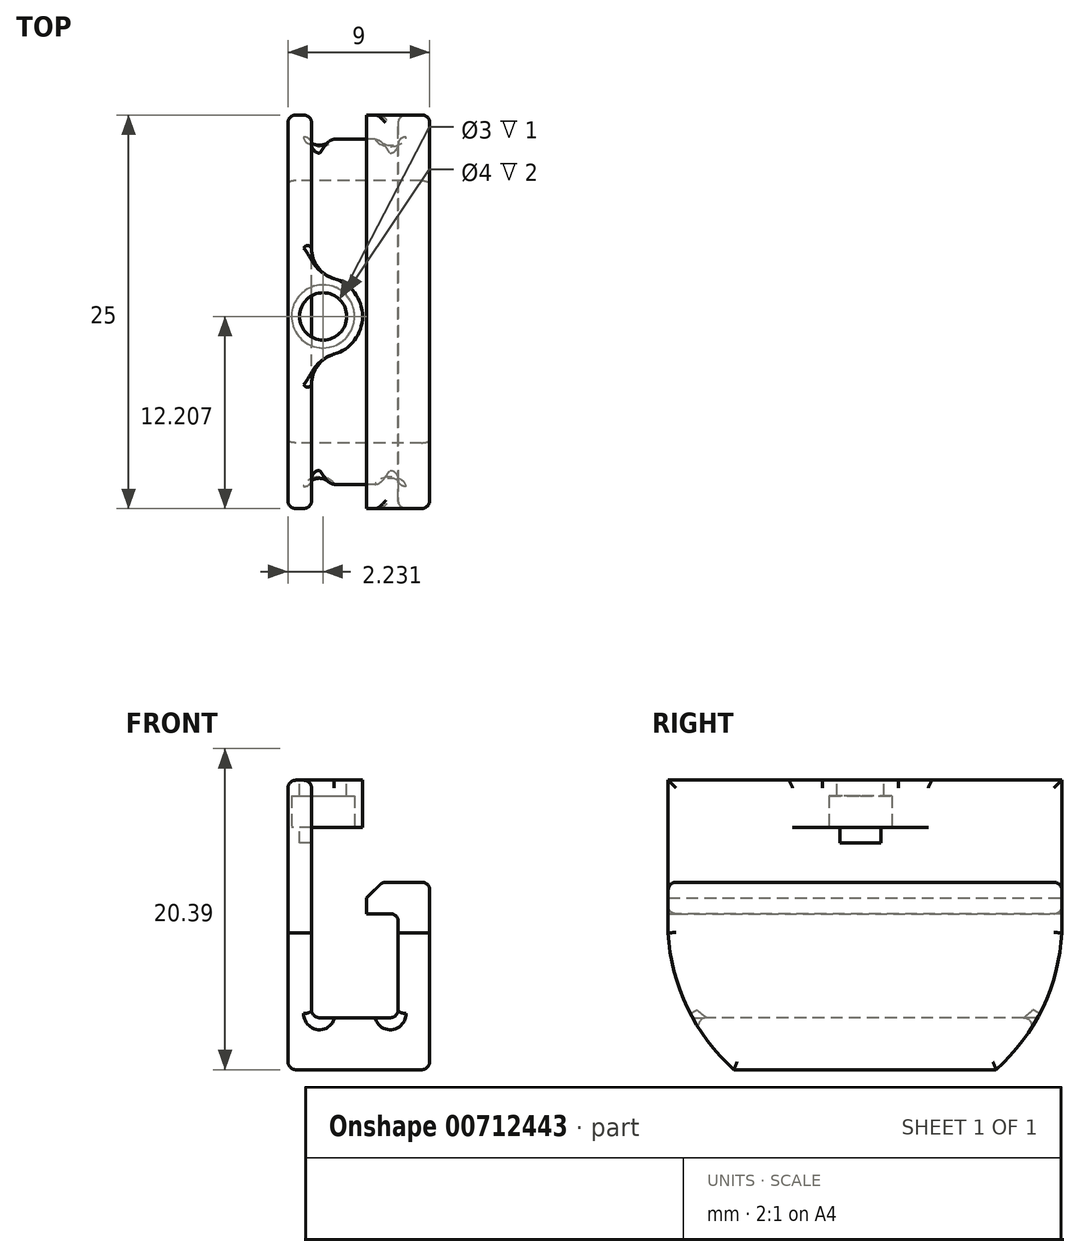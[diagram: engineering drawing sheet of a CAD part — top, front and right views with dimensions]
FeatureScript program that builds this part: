
annotation { "Feature Type Name" : "Feature", "Feature Type Description" : "" }
export const myFeature = defineFeature(function(context is Context, id is Id, definition is map)
    precondition{}
    {
        {
            var Q0;
            Q0=qCreatedBy(makeId("Top.planeOp"),FACE);
            var sketch = newSketch(context, id + "F0", { "sketchPlane" : qUnion([Q0])});
            skCircle(sketch, "E0", {"center": v(0, 0) * mm, "radius": 3.5 * mm});
            skSolve(sketch);
        }
        {
            var Q0;
            Q0 = qSketchRegion(id + "F0", true);
            extrude(context, id + "F1", {"entities" : qUnion([Q0]), "depth" : 15 * mm, "offsetDistance" : 25 * mm});
        }
        {
            var Q0;
            Q0=makeQuery(id+"F1.opExtrude","CAP_FACE",FACE,{"disambiguationData":[OSD([sQuery(id+"F0.wireOp",EDGE,"E0")])],"isStart":false});
            var sketch = newSketch(context, id + "F2", { "sketchPlane" : qUnion([Q0])});
            skCircle(sketch, "E1", {"center": v(0, 0) * mm, "radius": 1.6 * mm});
            skSolve(sketch);
        }
        {
            var Q0;
            Q0 = qSketchRegion(id + "F2", true);
            extrude(context, id + "F3", {"entities" : qUnion([Q0]), "operationType" : NewBodyOperationType.REMOVE, "oppositeDirection" : true, "depth" : 25 * mm, "offsetDistance" : 25 * mm});
        }
        {
            var Q0;
            Q0=makeQuery(id+"F1.opExtrude","CAP_FACE",FACE,{"disambiguationData":[OSD([sQuery(id+"F0.wireOp",EDGE,"E0")])],"isStart":false});
            var sketch = newSketch(context, id + "F4", { "sketchPlane" : qUnion([Q0])});
            skLineSegment(sketch, "E2.bottom", {"start": v(3.28, 0) * mm, "end": v(12.28, 0) * mm});
            skLineSegment(sketch, "E2.top", {"start": v(3.28, -12.5) * mm, "end": v(12.28, -12.5) * mm});
            skLineSegment(sketch, "E2.left", {"start": v(3.28, 0) * mm, "end": v(3.28, -12.5) * mm});
            skLineSegment(sketch, "E2.right", {"start": v(12.28, 0) * mm, "end": v(12.28, -12.5) * mm});
            skLineSegment(sketch, "E3.top", {"start": v(3.28, 12.5) * mm, "end": v(12.28, 12.5) * mm});
            skLineSegment(sketch, "E3.left", {"start": v(3.28, 0) * mm, "end": v(3.28, 12.5) * mm});
            skLineSegment(sketch, "E3.right", {"start": v(12.28, 0) * mm, "end": v(12.28, 12.5) * mm});
            skSolve(sketch);
        }
        {
            var Q0;
            Q0 = qSketchRegion(id + "F4", true);
            extrude(context, id + "F5", {"entities" : qUnion([Q0]), "operationType" : NewBodyOperationType.ADD, "oppositeDirection" : true, "depth" : 25 * mm, "offsetDistance" : 25 * mm});
        }
        {
            var Q0;
            Q0=makeQuery(id+"F5.boolean.opBoolean","INTERSECT",EDGE,{"disambiguationData":[OD(1.0)],"derivedFrom":[makeQuery(id+"F1.opExtrude","SWEPT_FACE",FACE,{"disambiguationData":[OSD([sQuery(id+"F0.wireOp",EDGE,"E0")])]}),makeQuery(id+"F5.opExtrude","SWEPT_FACE",FACE,{"disambiguationData":[OSD([sQuery(id+"F4.wireOp",EDGE,"E2.left"),sQuery(id+"F4.wireOp",EDGE,"E3.left")])]})]});
            var Q1;
            Q1=makeQuery(id+"F5.boolean.opBoolean","INTERSECT",EDGE,{"disambiguationData":[OD(0.0)],"derivedFrom":[makeQuery(id+"F1.opExtrude","SWEPT_FACE",FACE,{"disambiguationData":[OSD([sQuery(id+"F0.wireOp",EDGE,"E0")])]}),makeQuery(id+"F5.opExtrude","SWEPT_FACE",FACE,{"disambiguationData":[OSD([sQuery(id+"F4.wireOp",EDGE,"E2.left"),sQuery(id+"F4.wireOp",EDGE,"E3.left")])]})]});
            fillet(context, id + "F6", {"entities" : qUnion([Q0, Q1]), "radius" : 5 * mm, "tangentPropagation" : true, "allowEdgeOverflow" : false});
        }
        {
            var Q0;
            Q0=makeQuery(id+"F1.opExtrude","CAP_FACE",FACE,{"disambiguationData":[OSD([sQuery(id+"F0.wireOp",EDGE,"E0")])],"isStart":true});
            var sketch = newSketch(context, id + "F7", { "sketchPlane" : qUnion([Q0])});
            skCircle(sketch, "E4", {"center": v(0, 0) * mm, "radius": 2.5 * mm});
            skSolve(sketch);
        }
        {
            var Q0;
            Q0 = qSketchRegion(id + "F7", true);
            extrude(context, id + "F8", {"entities" : qUnion([Q0]), "operationType" : NewBodyOperationType.REMOVE, "oppositeDirection" : true, "depth" : 5 * mm, "offsetDistance" : 25 * mm});
        }
        {
            var Q0;
            Q0=makeQuery(id+"F5.opExtrude","SWEPT_FACE",FACE,{"disambiguationData":[OSD([sQuery(id+"F4.wireOp",EDGE,"E2.left"),sQuery(id+"F4.wireOp",EDGE,"E3.left")])]});
            var sketch = newSketch(context, id + "F9", { "sketchPlane" : qUnion([Q0])});
            skArc(sketch, "E5", {"start": v(-12.5, 0) * mm, "mid": v(-11.55, -5.48) * mm, "end": v(-8.32, -10) * mm});
            skArc(sketch, "E6", {"start": v(8.32, -10) * mm, "mid": v(11.55, -5.48) * mm, "end": v(12.5, 0) * mm});
            skLineSegment(sketch, "E7", {"start": v(-12.5, 0) * mm, "end": v(-12.5, -10) * mm});
            skLineSegment(sketch, "E8", {"start": v(-12.5, -10) * mm, "end": v(-8.32, -10) * mm});
            skLineSegment(sketch, "E9", {"start": v(12.5, 0) * mm, "end": v(12.5, -10) * mm});
            skLineSegment(sketch, "E10", {"start": v(12.5, -10) * mm, "end": v(8.32, -10) * mm});
            skSolve(sketch);
        }
        {
            var Q0;
            Q0 = qSketchRegion(id + "F9", true);
            extrude(context, id + "F10", {"entities" : qUnion([Q0]), "operationType" : NewBodyOperationType.REMOVE, "oppositeDirection" : true, "depth" : 25 * mm, "offsetDistance" : 25 * mm});
        }
        {
            var Q0;
            Q0=makeQuery(id+"F5.boolean.opBoolean","MERGE",FACE,{"derivedFrom":[makeQuery(id+"F1.opExtrude","CAP_FACE",FACE,{"disambiguationData":[OSD([sQuery(id+"F0.wireOp",EDGE,"E0")])],"isStart":false}),makeQuery(id+"F5.opExtrude","CAP_FACE",FACE,{"disambiguationData":[OSD([sQuery(id+"F4.wireOp",EDGE,"E2.top"),sQuery(id+"F4.wireOp",EDGE,"E2.left"),sQuery(id+"F4.wireOp",EDGE,"E2.right"),sQuery(id+"F4.wireOp",EDGE,"E3.top"),sQuery(id+"F4.wireOp",EDGE,"E3.left"),sQuery(id+"F4.wireOp",EDGE,"E3.right")])],"isStart":true})]});
            var sketch = newSketch(context, id + "F11", { "sketchPlane" : qUnion([Q0])});
            skLineSegment(sketch, "E11.bottom", {"start": v(4.78, 12.5) * mm, "end": v(10.28, 12.5) * mm});
            skLineSegment(sketch, "E11.top", {"start": v(4.78, -12.5) * mm, "end": v(10.28, -12.5) * mm});
            skLineSegment(sketch, "E11.left", {"start": v(4.78, 12.5) * mm, "end": v(4.78, -12.5) * mm});
            skLineSegment(sketch, "E11.right", {"start": v(10.28, 12.5) * mm, "end": v(10.28, -12.5) * mm});
            skSolve(sketch);
        }
        {
            var Q0;
            Q0 = qSketchRegion(id + "F11", true);
            extrude(context, id + "F12", {"entities" : qUnion([Q0]), "operationType" : NewBodyOperationType.REMOVE, "oppositeDirection" : true, "depth" : 21.7 * mm, "offsetDistance" : 25 * mm});
        }
        {
            var Q0;
            Q0=makeQuery(id+"F5.opExtrude","SWEPT_FACE",FACE,{"disambiguationData":[OSD([sQuery(id+"F4.wireOp",EDGE,"E2.right"),sQuery(id+"F4.wireOp",EDGE,"E3.right")])]});
            var sketch = newSketch(context, id + "F13", { "sketchPlane" : qUnion([Q0])});
            skLineSegment(sketch, "E12.bottom", {"start": v(-12.5, 15) * mm, "end": v(12.5, 15) * mm});
            skLineSegment(sketch, "E12.top", {"start": v(-12.5, 1.9) * mm, "end": v(12.5, 1.9) * mm});
            skLineSegment(sketch, "E12.left", {"start": v(-12.5, 15) * mm, "end": v(-12.5, 1.9) * mm});
            skLineSegment(sketch, "E12.right", {"start": v(12.5, 15) * mm, "end": v(12.5, 1.9) * mm});
            skSolve(sketch);
        }
        {
            var Q0;
            Q0 = qSketchRegion(id + "F13", true);
            extrude(context, id + "F14", {"entities" : qUnion([Q0]), "operationType" : NewBodyOperationType.REMOVE, "oppositeDirection" : true, "depth" : 3 * mm, "offsetDistance" : 25 * mm});
        }
        {
            var Q0;
            {var subQ5=sQuery(id+"F4.wireOp",EDGE,"E2.top");Q0=makeQuery(id+"F12.boolean.opBoolean","SPLIT",FACE,{"disambiguationData":[TD([makeQuery(id+"F12.opExtrude","SWEPT_FACE",FACE,{"disambiguationData":[OSD([sQuery(id+"F11.wireOp",EDGE,"E11.right")])]})])],"derivedFrom":makeQuery(id+"F5.opExtrude","SWEPT_FACE",FACE,{"disambiguationData":[OSD([subQ5])]})});}
            var sketch = newSketch(context, id + "F15", { "sketchPlane" : qUnion([Q0])});
            skLineSegment(sketch, "E13.bottom", {"start": v(12.28, 1.9) * mm, "end": v(8.28, 1.9) * mm});
            skLineSegment(sketch, "E13.top", {"start": v(12.28, -0.1) * mm, "end": v(8.28, -0.1) * mm});
            skLineSegment(sketch, "E13.left", {"start": v(12.28, 1.9) * mm, "end": v(12.28, -0.1) * mm});
            skLineSegment(sketch, "E13.right", {"start": v(8.28, 1.9) * mm, "end": v(8.28, -0.1) * mm});
            skSolve(sketch);
        }
        {
            var Q0;
            Q0 = qSketchRegion(id + "F15", true);
            extrude(context, id + "F16", {"entities" : qUnion([Q0]), "operationType" : NewBodyOperationType.ADD, "oppositeDirection" : true, "depth" : 25 * mm, "offsetDistance" : 25 * mm});
        }
        {
            var Q0;
            Q0=makeQuery(id+"F16.opExtrude","SWEPT_EDGE",EDGE,{"disambiguationData":[OSD([sQuery(id+"F15.wireOp",EDGE,"E13.bottom"),sQuery(id+"F15.wireOp",EDGE,"E13.right")])]});
            chamfer(context, id + "F17", {"entities" : qUnion([Q0]), "width" : 1 * mm, "tangentPropagation" : true});
        }
        {
            var Q0;
            {var subQ2=sQuery(id+"F4.wireOp",EDGE,"E3.top");Q0=makeQuery(id+"F12.boolean.opBoolean","SPLIT",FACE,{"disambiguationData":[TD([makeQuery(id+"F12.opExtrude","SWEPT_FACE",FACE,{"disambiguationData":[OSD([sQuery(id+"F11.wireOp",EDGE,"E11.left")])]})])],"derivedFrom":makeQuery(id+"F5.opExtrude","SWEPT_FACE",FACE,{"disambiguationData":[OSD([subQ2])]})});}
            var sketch = newSketch(context, id + "F18", { "sketchPlane" : qUnion([Q0])});
            skLineSegment(sketch, "E14.bottom", {"start": v(-7.78, 16.39) * mm, "end": v(8.9, 16.39) * mm});
            skLineSegment(sketch, "E14.top", {"start": v(-7.78, 8.39) * mm, "end": v(8.9, 8.39) * mm});
            skLineSegment(sketch, "E14.left", {"start": v(-7.78, 16.39) * mm, "end": v(-7.78, 8.39) * mm});
            skLineSegment(sketch, "E14.right", {"start": v(8.9, 16.39) * mm, "end": v(8.9, 8.39) * mm});
            skSolve(sketch);
        }
        {
            var Q0;
            Q0 = qSketchRegion(id + "F18", true);
            extrude(context, id + "F19", {"entities" : qUnion([Q0]), "operationType" : NewBodyOperationType.REMOVE, "oppositeDirection" : true, "depth" : 25 * mm, "offsetDistance" : 25 * mm});
        }
        {
            var Q0;
            Q0=makeQuery(id+"F5.opExtrude","CAP_EDGE",EDGE,{"disambiguationData":[OSD([sQuery(id+"F4.wireOp",EDGE,"E2.right"),sQuery(id+"F4.wireOp",EDGE,"E3.right")])],"isStart":false});
            var Q1;
            Q1=makeQuery(id+"F5.opExtrude","CAP_EDGE",EDGE,{"disambiguationData":[OSD([sQuery(id+"F4.wireOp",EDGE,"E2.left"),sQuery(id+"F4.wireOp",EDGE,"E3.left")])],"isStart":false});
            var Q2;
            Q2=makeQuery(id+"F5.opExtrude","SWEPT_FACE",FACE,{"disambiguationData":[OSD([sQuery(id+"F4.wireOp",EDGE,"E2.left"),sQuery(id+"F4.wireOp",EDGE,"E3.left")])]});
            var Q3;
            Q3=makeQuery(id+"F5.opExtrude","SWEPT_FACE",FACE,{"disambiguationData":[OSD([sQuery(id+"F4.wireOp",EDGE,"E2.right"),sQuery(id+"F4.wireOp",EDGE,"E3.right")])]});
            var Q4;
            Q4=makeQuery(id+"F12.boolean.opBoolean","COPY",FACE,{"derivedFrom":makeQuery(id+"F12.opExtrude","SWEPT_FACE",FACE,{"disambiguationData":[OSD([sQuery(id+"F11.wireOp",EDGE,"E11.left")])]})});
            var Q5;
            Q5=makeQuery(id+"F12.boolean.opBoolean","COPY",FACE,{"derivedFrom":makeQuery(id+"F12.opExtrude","SWEPT_FACE",FACE,{"disambiguationData":[OSD([sQuery(id+"F11.wireOp",EDGE,"E11.right")])]})});
            var Q6;
            Q6=makeQuery(id+"F16.boolean.opBoolean","MERGE",FACE,{"derivedFrom":[makeQuery(id+"F14.boolean.opBoolean","COPY",FACE,{"derivedFrom":makeQuery(id+"F14.opExtrude","SWEPT_FACE",FACE,{"disambiguationData":[OSD([sQuery(id+"F13.wireOp",EDGE,"E12.top")])]})}),makeQuery(id+"F16.opExtrude","SWEPT_FACE",FACE,{"disambiguationData":[OSD([sQuery(id+"F15.wireOp",EDGE,"E13.bottom")])]})]});
            fillet(context, id + "F20", {"entities" : qUnion([Q0, Q1, Q2, Q3, Q4, Q5, Q6]), "radius" : 0.5 * mm, "tangentPropagation" : true, "allowEdgeOverflow" : false});
        }
        {
            var Q0;
            Q0=makeQuery(id+"F19.boolean.opBoolean","COPY",FACE,{"derivedFrom":makeQuery(id+"F19.opExtrude","SWEPT_FACE",FACE,{"disambiguationData":[OSD([sQuery(id+"F18.wireOp",EDGE,"E14.top")])]})});
            var sketch = newSketch(context, id + "F21", { "sketchPlane" : qUnion([Q0])});
            skCircle(sketch, "E15", {"center": v(5.51, -0.3) * mm, "radius": 2.5 * mm});
            skSolve(sketch);
        }
        {
            var Q0;
            Q0 = qSketchRegion(id + "F21", true);
            extrude(context, id + "F22", {"entities" : qUnion([Q0]), "operationType" : NewBodyOperationType.ADD, "oppositeDirection" : true, "depth" : 3 * mm, "offsetDistance" : 25 * mm});
        }
        {
            var Q0;
            Q0=makeQuery(id+"F22.boolean.opBoolean","INTERSECT",EDGE,{"disambiguationData":[OD(0.0)],"derivedFrom":[makeQuery(id+"F12.boolean.opBoolean","COPY",FACE,{"derivedFrom":makeQuery(id+"F12.opExtrude","SWEPT_FACE",FACE,{"disambiguationData":[OSD([sQuery(id+"F11.wireOp",EDGE,"E11.left")])]})}),makeQuery(id+"F22.opExtrude","SWEPT_FACE",FACE,{"disambiguationData":[OSD([sQuery(id+"F21.wireOp",EDGE,"E15")])]})]});
            var Q1;
            Q1=makeQuery(id+"F22.boolean.opBoolean","INTERSECT",EDGE,{"disambiguationData":[OD(1.0)],"derivedFrom":[makeQuery(id+"F12.boolean.opBoolean","COPY",FACE,{"derivedFrom":makeQuery(id+"F12.opExtrude","SWEPT_FACE",FACE,{"disambiguationData":[OSD([sQuery(id+"F11.wireOp",EDGE,"E11.left")])]})}),makeQuery(id+"F22.opExtrude","SWEPT_FACE",FACE,{"disambiguationData":[OSD([sQuery(id+"F21.wireOp",EDGE,"E15")])]})]});
            fillet(context, id + "F23", {"entities" : qUnion([Q0, Q1]), "radius" : 2 * mm, "tangentPropagation" : true, "allowEdgeOverflow" : false});
        }
        {
            var Q0;
            Q0=makeQuery(id+"F22.boolean.opBoolean","MERGE",FACE,{"derivedFrom":[makeQuery(id+"F19.boolean.opBoolean","COPY",FACE,{"derivedFrom":makeQuery(id+"F19.opExtrude","SWEPT_FACE",FACE,{"disambiguationData":[OSD([sQuery(id+"F18.wireOp",EDGE,"E14.top")])]})}),makeQuery(id+"F22.opExtrude","CAP_FACE",FACE,{"disambiguationData":[OSD([sQuery(id+"F21.wireOp",EDGE,"E15")])],"isStart":true})]});
            var sketch = newSketch(context, id + "F24", { "sketchPlane" : qUnion([Q0])});
            skCircle(sketch, "E16", {"center": v(5.51, -0.3) * mm, "radius": 1.5 * mm});
            skSolve(sketch);
        }
        {
            var Q0;
            Q0 = qSketchRegion(id + "F24", true);
            extrude(context, id + "F25", {"entities" : qUnion([Q0]), "operationType" : NewBodyOperationType.REMOVE, "oppositeDirection" : true, "depth" : 4 * mm, "offsetDistance" : 25 * mm});
        }
        {
            var Q0;
            Q0=makeQuery(id+"F22.opExtrude","CAP_FACE",FACE,{"disambiguationData":[OSD([sQuery(id+"F21.wireOp",EDGE,"E15")])],"isStart":false});
            var sketch = newSketch(context, id + "F26", { "sketchPlane" : qUnion([Q0])});
            skCircle(sketch, "E17", {"center": v(5.51, 0.3) * mm, "radius": 2 * mm});
            skSolve(sketch);
        }
        {
            var Q0;
            Q0 = qSketchRegion(id + "F26", true);
            extrude(context, id + "F27", {"entities" : qUnion([Q0]), "operationType" : NewBodyOperationType.REMOVE, "oppositeDirection" : true, "depth" : 2 * mm, "offsetDistance" : 25 * mm});
        }
        {
            var Q0;
            Q0=makeQuery(id+"F5.opExtrude","SWEPT_FACE",FACE,{"disambiguationData":[OSD([sQuery(id+"F4.wireOp",EDGE,"E2.left"),sQuery(id+"F4.wireOp",EDGE,"E3.left")])]});
            var sketch = newSketch(context, id + "F28", { "sketchPlane" : qUnion([Q0])});
            skLineSegment(sketch, "E18.bottom", {"start": v(-9.98, 11.53) * mm, "end": v(10.31, 11.53) * mm});
            skLineSegment(sketch, "E18.top", {"start": v(-9.98, -3.71) * mm, "end": v(10.31, -3.71) * mm});
            skLineSegment(sketch, "E18.left", {"start": v(-9.98, 11.53) * mm, "end": v(-9.98, -3.71) * mm});
            skLineSegment(sketch, "E18.right", {"start": v(10.31, 11.53) * mm, "end": v(10.31, -3.71) * mm});
            skSolve(sketch);
        }
        {
            var Q0;
            Q0 = qSketchRegion(id + "F28", true);
            extrude(context, id + "F29", {"entities" : qUnion([Q0]), "operationType" : NewBodyOperationType.REMOVE, "depth" : 8.1 * mm, "offsetDistance" : 25 * mm});
        }
        {
            var Q0;
            Q0=makeQuery(id+"F29.boolean.opBoolean","INTERSECT",EDGE,{"derivedFrom":[makeQuery(id+"F22.boolean.opBoolean","MERGE",FACE,{"derivedFrom":[makeQuery(id+"F19.boolean.opBoolean","COPY",FACE,{"derivedFrom":makeQuery(id+"F19.opExtrude","SWEPT_FACE",FACE,{"disambiguationData":[OSD([sQuery(id+"F18.wireOp",EDGE,"E14.top")])]})}),makeQuery(id+"F22.opExtrude","CAP_FACE",FACE,{"disambiguationData":[OSD([sQuery(id+"F21.wireOp",EDGE,"E15")])],"isStart":true})]}),makeQuery(id+"F29.opExtrude","CAP_FACE",FACE,{"disambiguationData":[OSD([sQuery(id+"F28.wireOp",EDGE,"E18.bottom"),sQuery(id+"F28.wireOp",EDGE,"E18.top"),sQuery(id+"F28.wireOp",EDGE,"E18.left"),sQuery(id+"F28.wireOp",EDGE,"E18.right")])],"isStart":true})]});
            fillet(context, id + "F30", {"entities" : qUnion([Q0]), "radius" : 0.5 * mm, "tangentPropagation" : true, "allowEdgeOverflow" : false});
        }
    });
